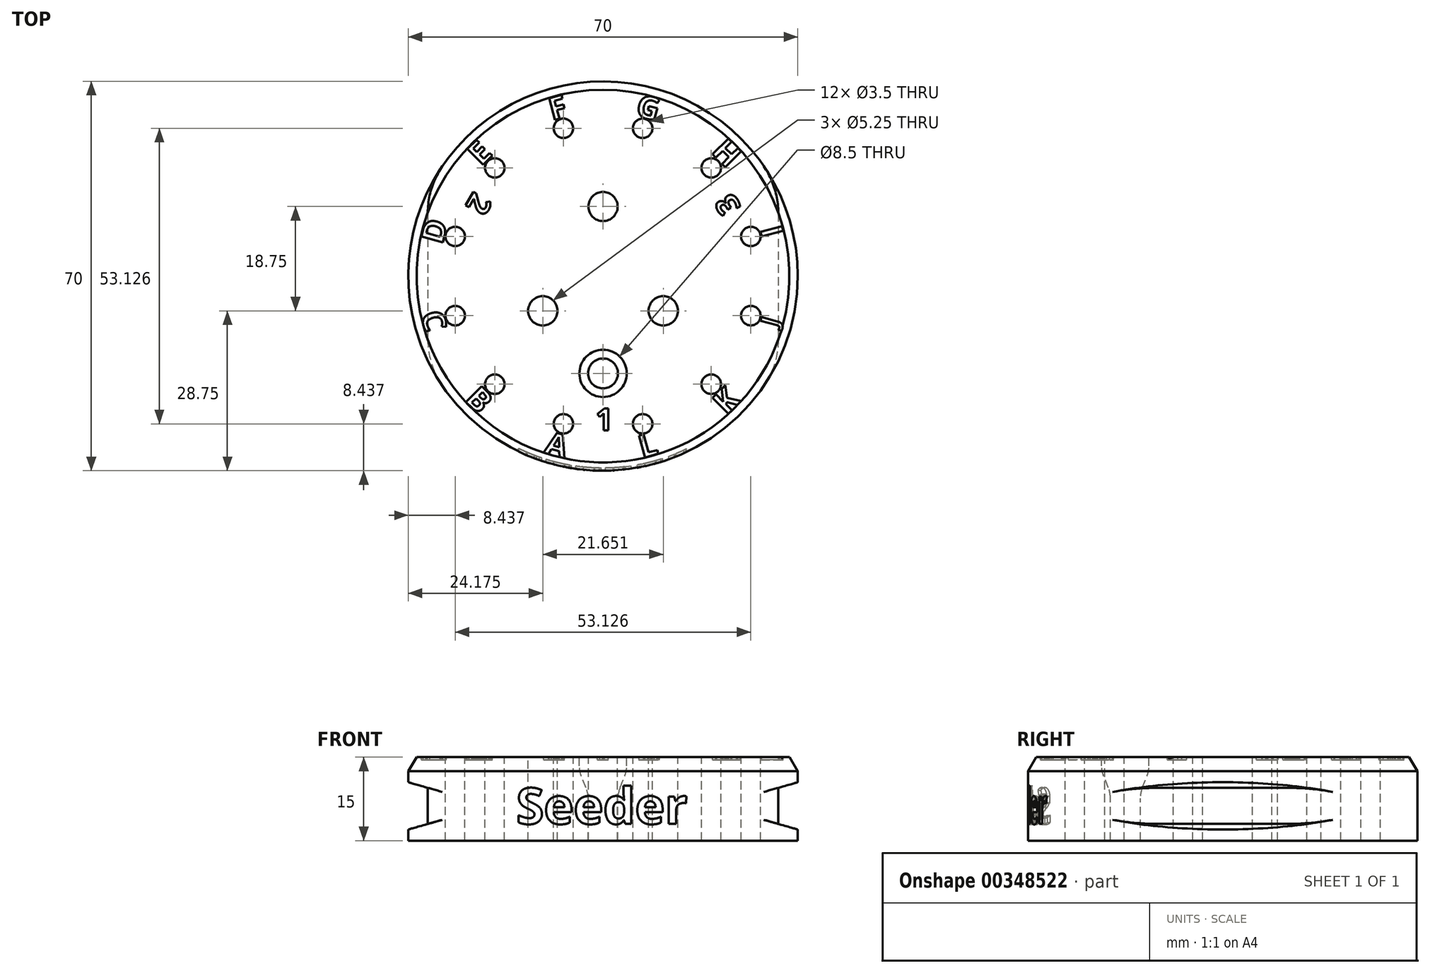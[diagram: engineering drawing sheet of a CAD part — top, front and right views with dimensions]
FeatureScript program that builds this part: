
annotation { "Feature Type Name" : "Feature", "Feature Type Description" : "" }
export const myFeature = defineFeature(function(context is Context, id is Id, definition is map)
    precondition{}
    {
        {
            var Q0;
            Q0=qCreatedBy(makeId("Top.planeOp"),FACE);
            var sketch = newSketch(context, id + "F0", { "sketchPlane" : qUnion([Q0])});
            skCircle(sketch, "E0", {"center": v(0, 0) * mm, "radius": 35 * mm});
            skSolve(sketch);
        }
        {
            var Q0;
            Q0=qSketchRegion(id+"F0",true);
            extrude(context, id + "F1", {"entities" : qUnion([Q0]), "depth" : 15 * mm});
        }
        {
            var Q0;
            Q0=qCreatedBy(makeId("Front.planeOp"),FACE);
            var sketch = newSketch(context, id + "F2", { "sketchPlane" : qUnion([Q0])});
            skText(sketch, "E1", { "text": "Seeder", "fontName": "OpenSans-Bold.ttf"});
            const initialGuessF2  = {"E1": [-0.0156, 0.003, 1, 0, 0.0065]};
            skSetInitialGuess(sketch, initialGuessF2);
            skSolve(sketch);
        }
        {
            var Q0;
            Q0=qSketchRegion(id+"F2",true);
            var Q1;
            Q1=makeQuery(id+"F1.opExtrude","SWEPT_FACE",FACE,{"disambiguationData":[OSD([sQuery(id+"F0.wireOp",EDGE,"E0")])]});
            extrude(context, id + "F3", {"entities" : qUnion([Q0]), "operationType" : NewBodyOperationType.REMOVE, "endBound" : BoundingType.THROUGH_ALL, "endBoundEntityFace" : qUnion([Q1]), "depth" : 25 * mm});
        }
        {
            var Q0;
            Q0=makeQuery(id+"F1.opExtrude","CAP_FACE",FACE,{"disambiguationData":[OSD([sQuery(id+"F0.wireOp",EDGE,"E0")])],"isStart":false});
            var sketch = newSketch(context, id + "F4", { "sketchPlane" : qUnion([Q0])});
            skCircle(sketch, "E2", {"center": v(0, 0) * mm, "radius": 34.5 * mm});
            skSolve(sketch);
        }
        {
            var Q0;
            Q0=qSketchRegion(id+"F4",true);
            var Q1;
            Q1=makeQuery(id+"F1.opExtrude","CAP_FACE",FACE,{"disambiguationData":[OSD([sQuery(id+"F0.wireOp",EDGE,"E0")])],"isStart":true});
            extrude(context, id + "F5", {"entities" : qUnion([Q0]), "operationType" : NewBodyOperationType.ADD, "endBound" : BoundingType.UP_TO_SURFACE, "oppositeDirection" : true, "endBoundEntityFace" : qUnion([Q1]), "depth" : 25 * mm});
        }
        {
            var Q0;
            Q0=qCreatedBy(makeId("Front.planeOp"),FACE);
            var sketch = newSketch(context, id + "F6", { "sketchPlane" : qUnion([Q0])});
            skLineSegment(sketch, "E3", {"start": v(-35, 10.5) * mm, "end": v(-35, 2) * mm});
            skLineSegment(sketch, "E4", {"start": v(-35, 2) * mm, "end": v(-31.5, 3) * mm});
            skLineSegment(sketch, "E5", {"start": v(-31.5, 3) * mm, "end": v(-31.5, 9.5) * mm});
            skLineSegment(sketch, "E6", {"start": v(-31.5, 9.5) * mm, "end": v(-35, 10.5) * mm});
            skLineSegment(sketch, "E7.MirrorCS", {"start": v(35, 10.5) * mm, "end": v(35, 2) * mm});
            skLineSegment(sketch, "E8.MirrorCS", {"start": v(31.5, 9.5) * mm, "end": v(35, 10.5) * mm});
            skLineSegment(sketch, "E9.MirrorCS", {"start": v(35, 2) * mm, "end": v(31.5, 3) * mm});
            skLineSegment(sketch, "E10.MirrorCS", {"start": v(31.5, 3) * mm, "end": v(31.5, 9.5) * mm});
            skSolve(sketch);
        }
        {
            var Q0;
            Q0=qSketchRegion(id+"F6",true);
            extrude(context, id + "F7", {"entities" : qUnion([Q0]), "operationType" : NewBodyOperationType.REMOVE, "endBound" : BoundingType.THROUGH_ALL, "oppositeDirection" : true, "depth" : 25 * mm, "hasSecondDirection" : true, "secondDirectionBound" : SecondDirectionBoundingType.THROUGH_ALL, "secondDirectionOppositeDirection" : false, "secondDirectionDepth" : 25 * mm});
        }
        {
            var Q0;
            {var subQ0=sQuery(id+"F0.wireOp",EDGE,"E0");Q0=makeQuery(id+"F7.boolean.opBoolean","INTERSECT",EDGE,{"disambiguationData":[OD(0.0)],"derivedFrom":[makeQuery(id+"F3.boolean.opBoolean","SPLIT",FACE,{"disambiguationData":[TD([makeQuery(id+"F1.opExtrude","CAP_FACE",FACE,{"disambiguationData":[OSD([subQ0])],"isStart":true})])],"derivedFrom":makeQuery(id+"F1.opExtrude","SWEPT_FACE",FACE,{"disambiguationData":[OSD([subQ0])]})}),makeQuery(id+"F7.opExtrude","SWEPT_FACE",FACE,{"disambiguationData":[OSD([sQuery(id+"F6.wireOp",EDGE,"E5")])]})]});}
            var Q1;
            {var subQ0=sQuery(id+"F0.wireOp",EDGE,"E0");Q1=makeQuery(id+"F7.boolean.opBoolean","INTERSECT",EDGE,{"disambiguationData":[OD(0.0)],"derivedFrom":[makeQuery(id+"F3.boolean.opBoolean","SPLIT",FACE,{"disambiguationData":[TD([makeQuery(id+"F1.opExtrude","CAP_FACE",FACE,{"disambiguationData":[OSD([subQ0])],"isStart":true})])],"derivedFrom":makeQuery(id+"F1.opExtrude","SWEPT_FACE",FACE,{"disambiguationData":[OSD([subQ0])]})}),makeQuery(id+"F7.opExtrude","SWEPT_FACE",FACE,{"disambiguationData":[OSD([sQuery(id+"F6.wireOp",EDGE,"E10.MirrorCS")])]})]});}
            var Q2;
            {var subQ0=sQuery(id+"F0.wireOp",EDGE,"E0");Q2=makeQuery(id+"F7.boolean.opBoolean","INTERSECT",EDGE,{"disambiguationData":[OD(1.0)],"derivedFrom":[makeQuery(id+"F3.boolean.opBoolean","SPLIT",FACE,{"disambiguationData":[TD([makeQuery(id+"F1.opExtrude","CAP_FACE",FACE,{"disambiguationData":[OSD([subQ0])],"isStart":true})])],"derivedFrom":makeQuery(id+"F1.opExtrude","SWEPT_FACE",FACE,{"disambiguationData":[OSD([subQ0])]})}),makeQuery(id+"F7.opExtrude","SWEPT_FACE",FACE,{"disambiguationData":[OSD([sQuery(id+"F6.wireOp",EDGE,"E10.MirrorCS")])]})]});}
            var Q3;
            {var subQ0=sQuery(id+"F0.wireOp",EDGE,"E0");Q3=makeQuery(id+"F7.boolean.opBoolean","INTERSECT",EDGE,{"disambiguationData":[OD(1.0)],"derivedFrom":[makeQuery(id+"F3.boolean.opBoolean","SPLIT",FACE,{"disambiguationData":[TD([makeQuery(id+"F1.opExtrude","CAP_FACE",FACE,{"disambiguationData":[OSD([subQ0])],"isStart":true})])],"derivedFrom":makeQuery(id+"F1.opExtrude","SWEPT_FACE",FACE,{"disambiguationData":[OSD([subQ0])]})}),makeQuery(id+"F7.opExtrude","SWEPT_FACE",FACE,{"disambiguationData":[OSD([sQuery(id+"F6.wireOp",EDGE,"E5")])]})]});}
            fillet(context, id + "F8", {"entities" : qUnion([Q0, Q1, Q2, Q3]), "radius" : 15 * mm, "tangentPropagation" : true, "allowEdgeOverflow" : false});
        }
        {
            var Q0;
            Q0=makeQuery(id+"F1.opExtrude","CAP_FACE",FACE,{"disambiguationData":[OSD([sQuery(id+"F0.wireOp",EDGE,"E0")])],"isStart":false});
            var sketch = newSketch(context, id + "F9", { "sketchPlane" : qUnion([Q0])});
            skCircle(sketch, "E11", {"center": v(0, 12.5) * mm, "radius": 2.62 * mm});
            skCircle(sketch, "E12.1.0", {"center": v(-10.83, -6.25) * mm, "radius": 2.62 * mm});
            skCircle(sketch, "E12.2.0", {"center": v(10.83, -6.25) * mm, "radius": 2.62 * mm});
            skPoint(sketch, "E12.center", {"position": v(0, 0) * mm});
            skCircle(sketch, "E13", {"center": v(0, 0) * mm, "radius": 12.5 * mm, "construction": true});
            skSolve(sketch);
        }
        {
            var Q0;
            Q0=qSketchRegion(id+"F9",true);
            extrude(context, id + "F10", {"entities" : qUnion([Q0]), "operationType" : NewBodyOperationType.REMOVE, "endBound" : BoundingType.THROUGH_ALL, "oppositeDirection" : true, "depth" : 25 * mm});
        }
        {
            var Q0;
            Q0=makeQuery(id+"F1.opExtrude","CAP_FACE",FACE,{"disambiguationData":[OSD([sQuery(id+"F0.wireOp",EDGE,"E0")])],"isStart":false});
            var sketch = newSketch(context, id + "F11", { "sketchPlane" : qUnion([Q0])});
            skCircle(sketch, "E14", {"center": v(0, -17.5) * mm, "radius": 2.68 * mm});
            skCircle(sketch, "E15", {"center": v(0, 0) * mm, "radius": 17.5 * mm, "construction": true});
            skSolve(sketch);
        }
        {
            var Q0;
            Q0=qSketchRegion(id+"F11",true);
            extrude(context, id + "F12", {"entities" : qUnion([Q0]), "operationType" : NewBodyOperationType.REMOVE, "endBound" : BoundingType.THROUGH_ALL, "oppositeDirection" : true, "depth" : 25 * mm});
        }
        {
            var Q0;
            Q0=makeQuery(id+"F1.opExtrude","CAP_FACE",FACE,{"disambiguationData":[OSD([sQuery(id+"F0.wireOp",EDGE,"E0")])],"isStart":false});
            var sketch = newSketch(context, id + "F13", { "sketchPlane" : qUnion([Q0])});
            skCircle(sketch, "E16", {"center": v(0, -17.5) * mm, "radius": 4.25 * mm});
            skSolve(sketch);
        }
        {
            var Q0;
            Q0=qSketchRegion(id+"F13",true);
            extrude(context, id + "F14", {"entities" : qUnion([Q0]), "operationType" : NewBodyOperationType.REMOVE, "oppositeDirection" : true, "depth" : 7.5 * mm});
        }
        {
            var Q0;
            Q0=makeQuery(id+"F14.boolean.opBoolean","COPY",EDGE,{"derivedFrom":makeQuery(id+"F14.opExtrude","CAP_EDGE",EDGE,{"disambiguationData":[OSD([sQuery(id+"F13.wireOp",EDGE,"E16")])],"isStart":false})});
            chamfer(context, id + "F15", {"entities" : qUnion([Q0]), "chamferType" : ChamferType.TWO_OFFSETS, "width1" : 5 * mm, "oppositeDirection" : true, "width2" : 2 * mm, "tangentPropagation" : true});
        }
        {
            var Q0;
            {var subQ0=sQuery(id+"F13.wireOp",EDGE,"E16");Q0=makeQuery(id+"F15.opChamfer","BLEND_EDGE",EDGE,{"blendedFrom":[makeQuery(id+"F14.boolean.opBoolean","COPY",EDGE,{"derivedFrom":makeQuery(id+"F14.opExtrude","CAP_EDGE",EDGE,{"disambiguationData":[OSD([subQ0])],"isStart":false})}),makeQuery(id+"F14.boolean.opBoolean","COPY",FACE,{"derivedFrom":makeQuery(id+"F14.opExtrude","SWEPT_FACE",FACE,{"disambiguationData":[OSD([subQ0])]})})],"blendedInto":[makeQuery(id+"F14.boolean.opBoolean","COPY",FACE,{"derivedFrom":makeQuery(id+"F14.opExtrude","SWEPT_FACE",FACE,{"disambiguationData":[OSD([subQ0])]})})]});}
            var Q1;
            Q1=makeQuery(id+"F15.opChamfer","BLEND_EDGE",EDGE,{"blendedFrom":[makeQuery(id+"F14.boolean.opBoolean","COPY",EDGE,{"derivedFrom":makeQuery(id+"F14.opExtrude","CAP_EDGE",EDGE,{"disambiguationData":[OSD([sQuery(id+"F13.wireOp",EDGE,"E16")])],"isStart":false})}),makeQuery(id+"F12.boolean.opBoolean","COPY",FACE,{"derivedFrom":makeQuery(id+"F12.opExtrude","SWEPT_FACE",FACE,{"disambiguationData":[OSD([sQuery(id+"F11.wireOp",EDGE,"E14")])]})})],"blendedInto":[makeQuery(id+"F12.boolean.opBoolean","COPY",FACE,{"derivedFrom":makeQuery(id+"F12.opExtrude","SWEPT_FACE",FACE,{"disambiguationData":[OSD([sQuery(id+"F11.wireOp",EDGE,"E14")])]})})]});
            fillet(context, id + "F16", {"entities" : qUnion([Q0, Q1]), "radius" : 5 * mm, "tangentPropagation" : true, "allowEdgeOverflow" : false});
        }
        {
            var Q0;
            Q0=makeQuery(id+"F1.opExtrude","CAP_FACE",FACE,{"disambiguationData":[OSD([sQuery(id+"F0.wireOp",EDGE,"E0")])],"isStart":false});
            var sketch = newSketch(context, id + "F17", { "sketchPlane" : qUnion([Q0])});
            skCircle(sketch, "E17", {"center": v(19.45, 19.45) * mm, "radius": 1.75 * mm});
            skCircle(sketch, "E18", {"center": v(0, 0) * mm, "radius": 27.5 * mm, "construction": true});
            skLineSegment(sketch, "E19", {"start": v(0, 0) * mm, "end": v(19.45, 19.45) * mm, "construction": true});
            skCircle(sketch, "E20.1.1", {"center": v(7.12, 26.56) * mm, "radius": 1.75 * mm});
            skCircle(sketch, "E20.2.1", {"center": v(-7.12, 26.56) * mm, "radius": 1.75 * mm});
            skCircle(sketch, "E20.3.1", {"center": v(-19.45, 19.45) * mm, "radius": 1.75 * mm});
            skCircle(sketch, "E20.4.1", {"center": v(-26.56, 7.12) * mm, "radius": 1.75 * mm});
            skCircle(sketch, "E20.5.1", {"center": v(-26.56, -7.12) * mm, "radius": 1.75 * mm});
            skCircle(sketch, "E20.6.1", {"center": v(-19.45, -19.45) * mm, "radius": 1.75 * mm});
            skCircle(sketch, "E20.7.1", {"center": v(-7.12, -26.56) * mm, "radius": 1.75 * mm});
            skCircle(sketch, "E20.8.1", {"center": v(7.12, -26.56) * mm, "radius": 1.75 * mm});
            skCircle(sketch, "E20.9.1", {"center": v(19.45, -19.45) * mm, "radius": 1.75 * mm});
            skCircle(sketch, "E20.10.1", {"center": v(26.56, -7.12) * mm, "radius": 1.75 * mm});
            skCircle(sketch, "E20.11.1", {"center": v(26.56, 7.12) * mm, "radius": 1.75 * mm});
            skSolve(sketch);
        }
        {
            var Q0;
            Q0=qSketchRegion(id+"F17",true);
            extrude(context, id + "F18", {"entities" : qUnion([Q0]), "operationType" : NewBodyOperationType.REMOVE, "endBound" : BoundingType.THROUGH_ALL, "oppositeDirection" : true, "depth" : 25 * mm});
        }
        {
            var Q0;
            Q0=makeQuery(id+"F1.opExtrude","CAP_EDGE",EDGE,{"disambiguationData":[OSD([sQuery(id+"F0.wireOp",EDGE,"E0")])],"isStart":false});
            chamfer(context, id + "F19", {"entities" : qUnion([Q0]), "chamferType" : ChamferType.TWO_OFFSETS, "width1" : 2.5 * mm, "oppositeDirection" : true, "width2" : 1.5 * mm, "tangentPropagation" : true});
        }
        {
            var Q0;
            Q0=makeQuery(id+"F1.opExtrude","CAP_FACE",FACE,{"disambiguationData":[OSD([sQuery(id+"F0.wireOp",EDGE,"E0")])],"isStart":false});
            var sketch = newSketch(context, id + "F20", { "sketchPlane" : qUnion([Q0])});
            skText(sketch, "E21", { "text": "A", "fontName": "OpenSans-Bold.ttf"});
            skText(sketch, "E22", { "text": "B", "fontName": "OpenSans-Bold.ttf"});
            skText(sketch, "E23", { "text": "C", "fontName": "OpenSans-Bold.ttf"});
            skText(sketch, "E24", { "text": "E", "fontName": "OpenSans-Bold.ttf"});
            skText(sketch, "E25", { "text": "F", "fontName": "OpenSans-Bold.ttf"});
            skText(sketch, "E26", { "text": "G", "fontName": "OpenSans-Bold.ttf"});
            skText(sketch, "E27", { "text": "H", "fontName": "OpenSans-Bold.ttf"});
            skText(sketch, "E28", { "text": "I", "fontName": "OpenSans-Bold.ttf"});
            skText(sketch, "E29", { "text": "J", "fontName": "OpenSans-Bold.ttf"});
            skText(sketch, "E30", { "text": "K", "fontName": "OpenSans-Bold.ttf"});
            skText(sketch, "E31", { "text": "L", "fontName": "OpenSans-Bold.ttf"});
            skText(sketch, "E32", { "text": "D", "fontName": "OpenSans-Bold.ttf"});
            skCircle(sketch, "E33", {"center": v(0, 0) * mm, "radius": 29.38 * mm, "construction": true});
            skText(sketch, "E34", { "text": "1", "fontName": "OpenSans-Bold.ttf"});
            skText(sketch, "E35", { "text": "2", "fontName": "OpenSans-Bold.ttf"});
            skText(sketch, "E36", { "text": "3", "fontName": "OpenSans-Bold.ttf"});
            skCircle(sketch, "E37", {"center": v(0, 0) * mm, "radius": 23.75 * mm, "construction": true});
            const initialGuessF20  = {"E21": [-0.0107, -0.03174, 0.96593, -0.25882, 0.00406], "E22": [-0.025, -0.02228, 0.7071, -0.7071, 0.00406], "E23": [-0.03278, -0.00684, 0.25882, -0.96593, 0.00406], "E24": [-0.0219, 0.01964, 0.7071, 0.7071, 0.00406], "E25": [-0.00914, 0.02796, 0.96593, 0.25882, 0.00406], "E26": [0.00567, 0.0289, 0.96593, -0.25882, 0.00406], "E27": [0.0193, 0.02225, 0.7071, -0.7071, 0.00406], "E28": [0.02815, 0.00844, 0.25882, -0.96593, 0.00406], "E29": [0.0313, -0.00927, 0.25882, 0.96593, 0.00325], "E30": [0.02219, -0.0251, 0.7071, 0.7071, 0.00406], "E31": [0.00703, -0.03273, 0.96593, 0.25882, 0.00406], "E32": [-0.02892, 0.00557, 0.25882, 0.96593, 0.00406], "E34": [-0.00133, -0.02775, 1, 0, 0.004], "E35": [-0.0232, 0.01533, -0.5, -0.86603, 0.004], "E36": [0.02486, 0.01244, -0.5, 0.86603, 0.004]};
            skSetInitialGuess(sketch, initialGuessF20);
            skSolve(sketch);
        }
        {
            var Q0;
            Q0=qSketchRegion(id+"F20",true);
            extrude(context, id + "F21", {"entities" : qUnion([Q0]), "operationType" : NewBodyOperationType.REMOVE, "oppositeDirection" : true, "depth" : .5 * mm});
        }
    });
